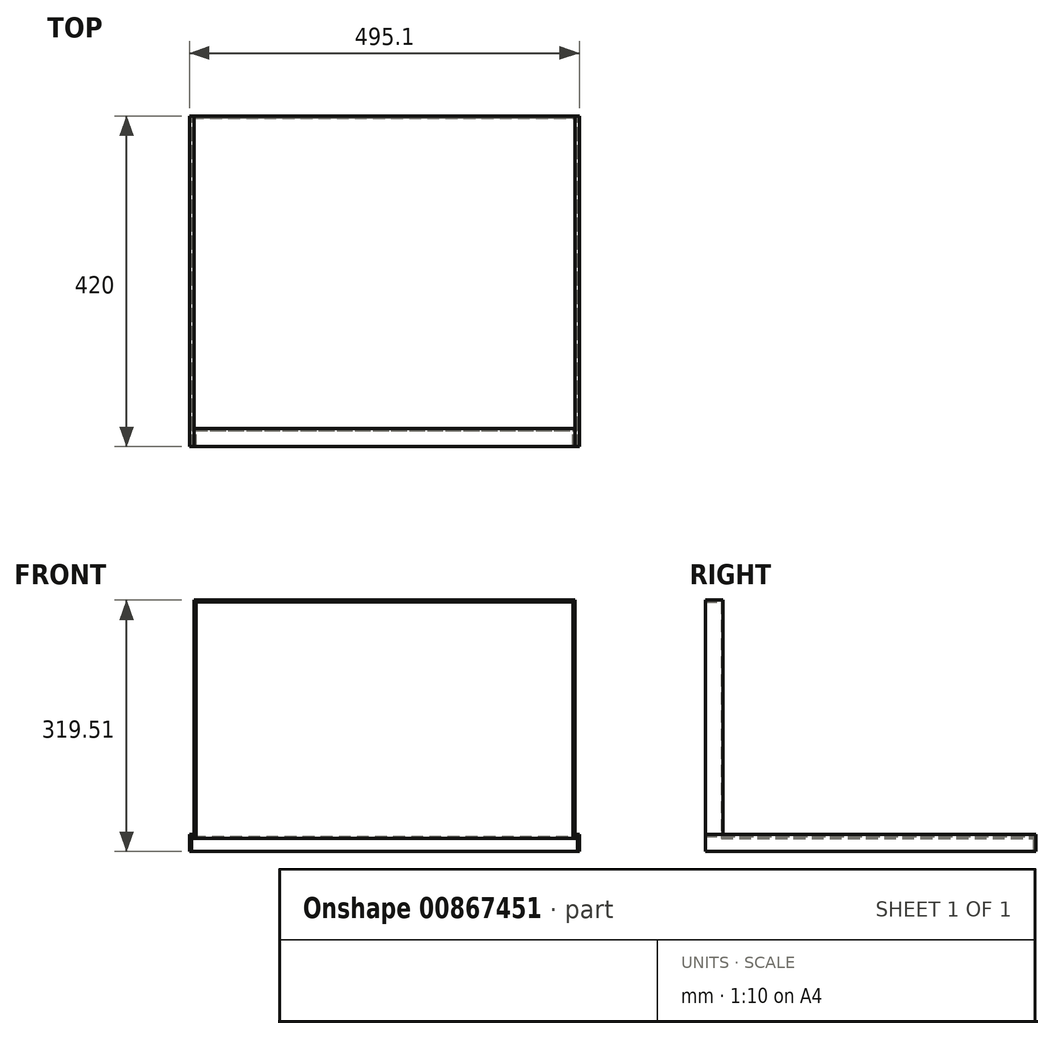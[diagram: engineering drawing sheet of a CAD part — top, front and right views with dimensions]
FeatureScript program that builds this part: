
annotation { "Feature Type Name" : "Feature", "Feature Type Description" : "" }
export const myFeature = defineFeature(function(context is Context, id is Id, definition is map)
    precondition{}
    {
        {
            var Q0;
            Q0=qCreatedBy(makeId("Front.planeOp"),FACE);
            var sketch = newSketch(context, id + "F0", { "sketchPlane" : qUnion([Q0])});
            skLineSegment(sketch, "E0", {"start": v(0, 19.51) * mm, "end": v(247.55, 19.51) * mm});
            skLineSegment(sketch, "E1", {"start": v(247.55, 19.51) * mm, "end": v(247.55, 0) * mm});
            skLineSegment(sketch, "E2", {"start": v(247.55, 0) * mm, "end": v(0, 0) * mm});
            skLineSegment(sketch, "E3", {"start": v(0, 0) * mm, "end": v(0, 29.85) * mm});
            skLineSegment(sketch, "E4.MirrorCS", {"start": v(0, 19.51) * mm, "end": v(-247.55, 19.51) * mm});
            skLineSegment(sketch, "E5.MirrorCS", {"start": v(-247.55, 0) * mm, "end": v(0, 0) * mm});
            skLineSegment(sketch, "E6.MirrorCS", {"start": v(-247.55, 19.51) * mm, "end": v(-247.55, 0) * mm});
            skLineSegment(sketch, "E7", {"start": v(-247.55, 19.51) * mm, "end": v(-247.55, 22.04) * mm});
            skLineSegment(sketch, "E8", {"start": v(-247.55, 22.04) * mm, "end": v(-241.89, 22.04) * mm});
            skLineSegment(sketch, "E9", {"start": v(-241.89, 22.04) * mm, "end": v(-241.89, 19.51) * mm});
            skLineSegment(sketch, "E10.MirrorCS", {"start": v(241.89, 22.04) * mm, "end": v(241.89, 19.51) * mm});
            skLineSegment(sketch, "E11.MirrorCS", {"start": v(247.55, 22.04) * mm, "end": v(241.89, 22.04) * mm});
            skLineSegment(sketch, "E12.MirrorCS", {"start": v(247.55, 19.51) * mm, "end": v(247.55, 22.04) * mm});
            skSolve(sketch);
        }
        {
            var Q0;
            Q0 = qSketchRegion(id + "F0", true);
            extrude(context, id + "F1", {"entities" : qUnion([Q0]), "endBound" : BoundingType.SYMMETRIC, "depth" : 420 * mm, "offsetDistance" : 25 * mm});
        }
        {
            var Q0;
            Q0=makeQuery(id+"F1.opExtrude","SWEPT_FACE",FACE,{"disambiguationData":[OSD([sQuery(id+"F0.wireOp",EDGE,"E0"),sQuery(id+"F0.wireOp",EDGE,"E4.MirrorCS")])]});
            var sketch = newSketch(context, id + "F2", { "sketchPlane" : qUnion([Q0])});
            skLineSegment(sketch, "E13.bottom", {"start": v(-241.89, -187.22) * mm, "end": v(241.89, -187.22) * mm});
            skLineSegment(sketch, "E13.top", {"start": v(-241.89, -210) * mm, "end": v(241.89, -210) * mm});
            skLineSegment(sketch, "E13.left", {"start": v(-241.89, -187.22) * mm, "end": v(-241.89, -210) * mm});
            skLineSegment(sketch, "E13.right", {"start": v(241.89, -187.22) * mm, "end": v(241.89, -210) * mm});
            skSolve(sketch);
        }
        {
            var Q0;
            Q0=makeQuery(id+"F2.imprint","IMPRINT",FACE,{"disambiguationData":[TD([[makeQuery(id+"F2.imprint","IMPRINT",EDGE,{"derivedFrom":sQuery(id+"F2.wireOp",EDGE,"E13.bottom")}),-1.0]])]});
            extrude(context, id + "F3", {"entities" : qUnion([Q0]), "operationType" : NewBodyOperationType.ADD, "depth" : 300 * mm, "offsetDistance" : 25 * mm});
        }
        {
            var Q0;
            Q0=makeQuery(id+"F1.opExtrude","SWEPT_FACE",FACE,{"disambiguationData":[OSD([sQuery(id+"F0.wireOp",EDGE,"E2"),sQuery(id+"F0.wireOp",EDGE,"E5.MirrorCS")])]});
            var Q1;
            Q1=makeQuery(id+"F3.boolean.opBoolean","MERGE",FACE,{"derivedFrom":[makeQuery(id+"F1.opExtrude","CAP_FACE",FACE,{"disambiguationData":[OSD([sQuery(id+"F0.wireOp",EDGE,"E0"),sQuery(id+"F0.wireOp",EDGE,"E1"),sQuery(id+"F0.wireOp",EDGE,"E2"),sQuery(id+"F0.wireOp",EDGE,"E4.MirrorCS"),sQuery(id+"F0.wireOp",EDGE,"E5.MirrorCS"),sQuery(id+"F0.wireOp",EDGE,"E6.MirrorCS"),sQuery(id+"F0.wireOp",EDGE,"E7"),sQuery(id+"F0.wireOp",EDGE,"E8"),sQuery(id+"F0.wireOp",EDGE,"E9"),sQuery(id+"F0.wireOp",EDGE,"E10.MirrorCS"),sQuery(id+"F0.wireOp",EDGE,"E11.MirrorCS"),sQuery(id+"F0.wireOp",EDGE,"E12.MirrorCS")])],"isStart":false}),makeQuery(id+"F3.opExtrude","SWEPT_FACE",FACE,{"disambiguationData":[OSD([sQuery(id+"F2.wireOp",EDGE,"E13.top")])]})]});
            shell(context, id + "F4", {"entities" : qUnion([Q0, Q1]), "thickness" : 2.5 * mm});
        }
    });
